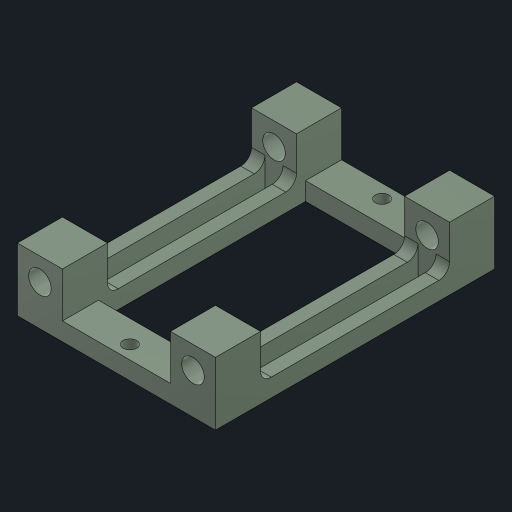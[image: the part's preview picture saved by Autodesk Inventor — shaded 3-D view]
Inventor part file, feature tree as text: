
AUTODESK INVENTOR PART (.ipt)
format: ipt  version: 2023 (Build 270158000, 158)  size: 235,008 bytes
history: native  units: in
note: dims shown in document units (in); Inventor stores cm internally (conversion verified against a paired STEP export)
features: sketch x4, extrude x4, other x3, mirror x2, hole x1, fillet x1, projected_geometry x1
ambient origin geometry x8: Origin, YZ Plane, XZ Plane, XY Plane, X Axis, Y Axis, Z Axis, Center Point
bodies: Body1 (feature_tree)
feature tree (16):
  other  "ソリッド1"
  sketch  "スケッチ1"
  extrude  "押し出し1"  Depth=0.9055in
  hole  "穴1"  [1 undecoded]
  extrude  "押し出し2"  Depth=0.1969in
  extrude  "押し出し5"  Depth=1.1024in
  mirror  "ミラー4"
  extrude  "押し出し6"  Depth=0.315in
  mirror  "ミラー5"
  fillet  "フィレット1"  Radius=0.0787in
  other  "作業平面1"
  other  "作業平面2"
  sketch  "スケッチ2"
  projected_geometry  "投影ループ1"
  sketch  "スケッチ6"
  sketch  "スケッチ7"
note: 1 required parameter value undecoded (feature->parameter linkage not recoverable at this tier; creation-order binding heuristic only, values carry confidence <= 0.55)
